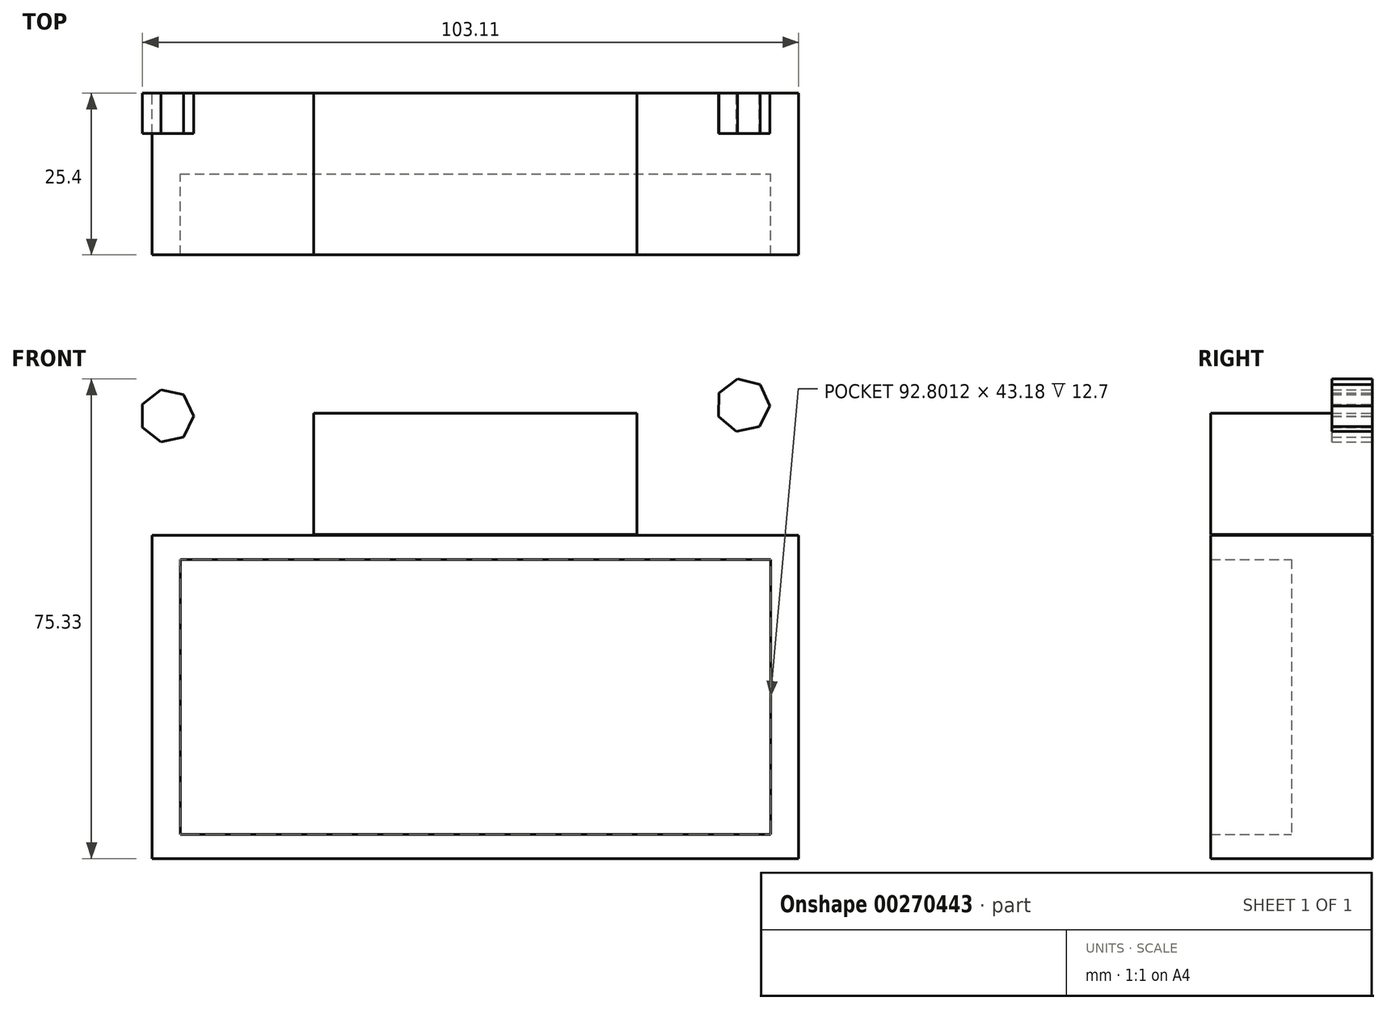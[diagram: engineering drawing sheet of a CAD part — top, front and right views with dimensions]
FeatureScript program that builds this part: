
annotation { "Feature Type Name" : "Feature", "Feature Type Description" : "" }
export const myFeature = defineFeature(function(context is Context, id is Id, definition is map)
    precondition{}
    {
        {
            var Q0;
            Q0=qCreatedBy(makeId("Front.planeOp"),FACE);
            var sketch = newSketch(context, id + "F0", { "sketchPlane" : qUnion([Q0])});
            skLineSegment(sketch, "E0.bottom", {"start": v(-50.8, 25.4) * mm, "end": v(50.8, 25.4) * mm});
            skLineSegment(sketch, "E0.top", {"start": v(-50.8, -25.4) * mm, "end": v(50.8, -25.4) * mm});
            skLineSegment(sketch, "E0.left", {"start": v(-50.8, 25.4) * mm, "end": v(-50.8, -25.4) * mm});
            skLineSegment(sketch, "E0.right", {"start": v(50.8, 25.4) * mm, "end": v(50.8, -25.4) * mm});
            skPoint(sketch, "E0.middle", {"position": v(0, 0) * mm});
            skLineSegment(sketch, "E1.bottom", {"start": v(-46.4, 21.59) * mm, "end": v(46.4, 21.59) * mm});
            skLineSegment(sketch, "E1.top", {"start": v(-46.4, -21.59) * mm, "end": v(46.4, -21.59) * mm});
            skLineSegment(sketch, "E1.left", {"start": v(-46.4, 21.59) * mm, "end": v(-46.4, -21.59) * mm});
            skLineSegment(sketch, "E1.right", {"start": v(46.4, 21.59) * mm, "end": v(46.4, -21.59) * mm});
            skLineSegment(sketch, "E2.bottom", {"start": v(-25.4, 44.53) * mm, "end": v(25.4, 44.53) * mm});
            skLineSegment(sketch, "E2.top", {"start": v(-25.4, 25.48) * mm, "end": v(25.4, 25.48) * mm});
            skLineSegment(sketch, "E2.left", {"start": v(-25.4, 44.53) * mm, "end": v(-25.4, 25.48) * mm});
            skLineSegment(sketch, "E2.right", {"start": v(25.4, 44.53) * mm, "end": v(25.4, 25.48) * mm});
            skPoint(sketch, "E2.middle", {"position": v(0, 35) * mm});
            skLineSegment(sketch, "E3", {"start": v(0, 44.53) * mm, "end": v(0, 25.48) * mm});
            skPoint(sketch, "E4", {"position": v(-13.69, 35.07) * mm});
            skPoint(sketch, "E5", {"position": v(13.69, 34.94) * mm});
            skSolve(sketch);
        }
        {
            var Q0;
            Q0=makeQuery(id+"F0.imprint","IMPRINT",FACE,{"disambiguationData":[TD([[makeQuery(id+"F0.imprint","IMPRINT",EDGE,{"derivedFrom":sQuery(id+"F0.wireOp",EDGE,"E1.bottom")}),-1.0]])]});
            extrude(context, id + "F1", {"entities" : qUnion([Q0]), "depth" : 12.7 * mm});
        }
        {
            var Q0;
            Q0=makeQuery(id+"F0.imprint","IMPRINT",FACE,{"disambiguationData":[TD([[makeQuery(id+"F0.imprint","IMPRINT",EDGE,{"derivedFrom":sQuery(id+"F0.wireOp",EDGE,"E0.bottom")}),-1.0]])]});
            var Q1;
            {var subQ0=sQuery(id+"F0.wireOp",EDGE,"E2.left");Q1=makeQuery(id+"F0.imprint","IMPRINT",FACE,{"disambiguationData":[TD([[makeQuery(id+"F0.imprint","IMPRINT",EDGE,{"derivedFrom":subQ0}),1.0]])]});}
            var Q2;
            {var subQ0=sQuery(id+"F0.wireOp",EDGE,"E2.right");Q2=makeQuery(id+"F0.imprint","IMPRINT",FACE,{"disambiguationData":[TD([[makeQuery(id+"F0.imprint","IMPRINT",EDGE,{"derivedFrom":subQ0}),-1.0]])]});}
            extrude(context, id + "F2", {"entities" : qUnion([Q0, Q1, Q2]), "operationType" : NewBodyOperationType.ADD, "depth" : 25.4 * mm});
        }
        {
            var Q0;
            Q0=makeQuery(id+"F2.opExtrude","CAP_FACE",FACE,{"disambiguationData":[OSD([sQuery(id+"F0.wireOp",EDGE,"E2.bottom"),sQuery(id+"F0.wireOp",EDGE,"E2.top"),sQuery(id+"F0.wireOp",EDGE,"E2.left"),sQuery(id+"F0.wireOp",EDGE,"E2.right")])],"isStart":false});
            var sketch = newSketch(context, id + "F3", { "sketchPlane" : qUnion([Q0])});
            skPoint(sketch, "E6.0", {"position": v(13.69, 34.94) * mm});
            skPoint(sketch, "E7.0", {"position": v(-13.69, 35.07) * mm});
            skSolve(sketch);
        }
        {
            var Q0;
            Q0=qCreatedBy(makeId("Front.planeOp"),FACE);
            var sketch = newSketch(context, id + "F4", { "sketchPlane" : qUnion([Q0])});
            skCircle(sketch, "E8.cCircle", {"center": v(-48.5, 44.14) * mm, "radius": 3.8 * mm, "construction": true});
            skLineSegment(sketch, "E8.0", {"start": v(-52.3, 42.3) * mm, "end": v(-52.3, 45.97) * mm});
            skLineSegment(sketch, "E8.1", {"start": v(-52.3, 45.97) * mm, "end": v(-49.44, 48.26) * mm});
            skLineSegment(sketch, "E8.2", {"start": v(-49.44, 48.26) * mm, "end": v(-45.86, 47.45) * mm});
            skLineSegment(sketch, "E8.3", {"start": v(-45.86, 47.45) * mm, "end": v(-44.27, 44.14) * mm});
            skLineSegment(sketch, "E8.4", {"start": v(-44.27, 44.14) * mm, "end": v(-45.86, 40.83) * mm});
            skLineSegment(sketch, "E8.5", {"start": v(-45.86, 40.83) * mm, "end": v(-49.44, 40.02) * mm});
            skLineSegment(sketch, "E8.6", {"start": v(-49.44, 40.02) * mm, "end": v(-52.3, 42.3) * mm});
            skPoint(sketch, "E8.0.midPoint", {"position": v(-52.3, 44.14) * mm});
            skCircle(sketch, "E9.cCircle", {"center": v(42.06, 45.8) * mm, "radius": 3.81 * mm, "construction": true});
            skPoint(sketch, "E9.cCircle.centerSnap0", {"position": v(-45.07, 45.8) * mm});
            skLineSegment(sketch, "E9.0", {"start": v(41.03, 41.69) * mm, "end": v(38.21, 44.04) * mm});
            skLineSegment(sketch, "E9.1", {"start": v(38.21, 44.04) * mm, "end": v(38.29, 47.7) * mm});
            skLineSegment(sketch, "E9.2", {"start": v(38.29, 47.7) * mm, "end": v(41.2, 49.93) * mm});
            skLineSegment(sketch, "E9.3", {"start": v(41.2, 49.93) * mm, "end": v(44.76, 49.04) * mm});
            skLineSegment(sketch, "E9.4", {"start": v(44.76, 49.04) * mm, "end": v(46.29, 45.7) * mm});
            skLineSegment(sketch, "E9.5", {"start": v(46.29, 45.7) * mm, "end": v(44.63, 42.43) * mm});
            skLineSegment(sketch, "E9.6", {"start": v(44.63, 42.43) * mm, "end": v(41.03, 41.69) * mm});
            skPoint(sketch, "E9.0.midPoint", {"position": v(39.62, 42.86) * mm});
            skSolve(sketch);
        }
        {
            var Q0;
            Q0 = qSketchRegion(id + "F4", true);
            extrude(context, id + "F5", {"entities" : qUnion([Q0]), "depth" : 6.35 * mm});
        }
    });
